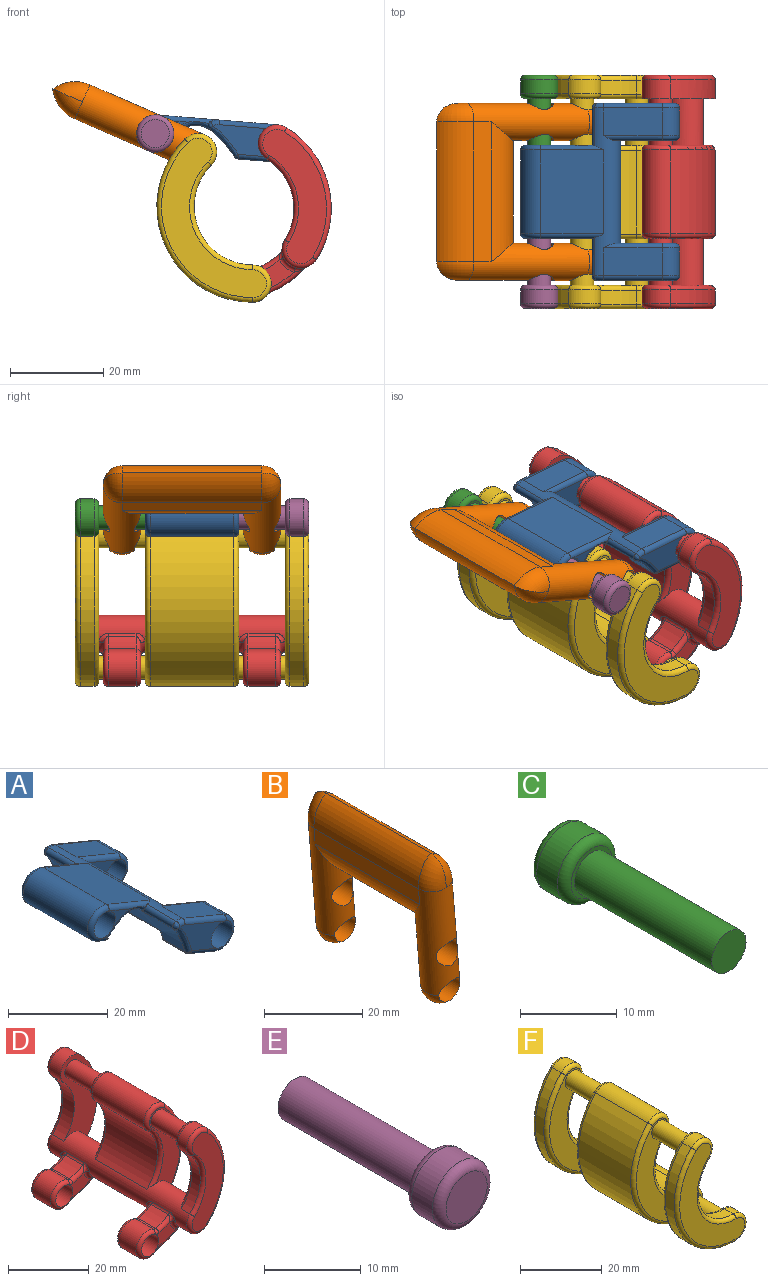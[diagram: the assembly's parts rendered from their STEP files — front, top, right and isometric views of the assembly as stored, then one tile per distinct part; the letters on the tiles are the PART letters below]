
ASSEMBLY  parts=6 mates=6
PART A: 60 faces, bbox 32.8x38x18.6 mm
  f0: plane 18x12.5mm, normal (0.38,0,0.92), area 243.4mm2, adj f2,f6,f49,f52
  f1: plane 18x1.85mm, normal (-0.38,0,-0.92), area 36.1mm2, adj f2,f51,f54,f57
  f2: cylinder r=4mm len=18mm, axis (0,1,0), area 226.2mm2, adj f0,f1,f50,f53
  f3: cylinder r=3mm len=20mm, axis (0,1,0), area 377mm2, adj f12,f19,f50,f53
  f4: extruded ~36x13.26mm, area 432.7mm2, adj f22,f27,f31,f34,f36,f38,f40,f43
  f5: plane 7.38x6mm, normal (-0.38,0,-0.92), area 47.9mm2, adj f9,f26,f30,f31
  f6: cylinder r=4mm len=36mm, axis (0,-1,0), area 200.1mm2, adj f0,f8,f11,f15,f18,f21,f22,f25
  f7: plane 13.07x10.59mm, normal (0,1,0), area 50.4mm2, adj f10,f20,f21,f26,f27
  f8: plane 10.18x9.36mm, normal (0,-1,0), area 38.9mm2, adj f6,f10,f25,f30,f34,f36
  f9: cylinder r=4mm len=7.7mm, axis (0,-1,0), area 75.4mm2, adj f5,f11,f23,f28
  f10: cylinder r=3mm len=8mm, axis (0,-1,0), area 150.8mm2, adj f7,f8,f23,f28
  f11: plane 11.67x6mm, normal (0.38,0,0.92), area 75.7mm2, adj f6,f9,f20,f25
  f12: plane 8.44x6.31mm, normal (0,1,0), area 8.5mm2, adj f3,f49,f51,f59
  f13: plane 7.38x6mm, normal (-0.38,0,-0.92), area 47.9mm2, adj f16,f37,f40,f42
  f14: plane 13.07x10.59mm, normal (0,-1,0), area 50.4mm2, adj f17,f42,f43,f47,f48
  f15: plane 10.18x9.36mm, normal (0,1,0), area 38.9mm2, adj f6,f17,f33,f36,f37,f38
  f16: cylinder r=4mm len=7.7mm, axis (0,1,0), area 75.4mm2, adj f13,f18,f35,f45
  f17: cylinder r=3mm len=8mm, axis (0,1,0), area 150.8mm2, adj f14,f15,f35,f45
  f18: plane 11.67x6mm, normal (0.38,0,0.92), area 75.7mm2, adj f6,f16,f33,f47
  f19: plane 8.44x6.31mm, normal (0,-1,0), area 8.5mm2, adj f3,f52,f54,f55
  f20: cylinder r=1mm len=12.05mm, axis (-0.92,0,0.38), area 19.8mm2, adj f7,f11,f21,f23
  f21: torus R=3mm, axis (0,1,0), area 2.7mm2, adj f6,f7,f20,f24
  f22: cylinder r=1mm len=9mm, axis (0,-1,0), area 18.2mm2, adj f4,f6,f24,f49,f59
  f23: torus R=3mm, axis (0,1,0), area 17.9mm2, adj f9,f10,f20,f26
  f24: sphere r=1mm, area 1.5mm2, adj f21,f22,f27
  f25: cylinder r=1mm len=12.05mm, axis (0.92,0,-0.38), area 17.8mm2, adj f6,f8,f11,f28
  f26: cylinder r=1mm len=7.76mm, axis (0.92,0,-0.38), area 12.5mm2, adj f5,f7,f23,f29
  f27: bspline ~9.21x4.77mm, area 12.6mm2, adj f4,f7,f24,f29
  f28: torus R=3mm, axis (0,1,0), area 17.9mm2, adj f9,f10,f25,f30
  f29: sphere r=1mm, area 0.6mm2, adj f26,f27,f31
  f30: cylinder r=1mm len=7.76mm, axis (-0.92,0,0.38), area 12.5mm2, adj f5,f8,f28,f32
  f31: cylinder r=1mm len=6mm, axis (0,-1,0), area 5.5mm2, adj f4,f5,f29,f32
  f32: sphere r=1mm, area 0.6mm2, adj f30,f31,f34
  f33: cylinder r=1mm len=12.05mm, axis (0.92,0,-0.38), area 17.8mm2, adj f6,f15,f18,f35
  f34: bspline ~5.09x2.5mm, area 3.5mm2, adj f4,f8,f32,f36
  f35: torus R=3mm, axis (0,-1,0), area 17.9mm2, adj f16,f17,f33,f37
  f36: cylinder r=1mm len=24mm, axis (0,-1,0), area 47.9mm2, adj f4,f6,f8,f15,f34,f38
  f37: cylinder r=1mm len=7.76mm, axis (-0.92,0,0.38), area 12.5mm2, adj f13,f15,f35,f39
  f38: bspline ~4.84x2.4mm, area 3.5mm2, adj f4,f15,f36,f39
  f39: sphere r=1mm, area 0.6mm2, adj f37,f38,f40
  f40: cylinder r=1mm len=6mm, axis (0,-1,0), area 5.5mm2, adj f4,f13,f39,f41
  f41: sphere r=1mm, area 0.6mm2, adj f40,f42,f43
  f42: cylinder r=1mm len=7.76mm, axis (0.92,0,-0.38), area 12.5mm2, adj f13,f14,f41,f45
  f43: bspline ~9.21x4.77mm, area 12.6mm2, adj f4,f14,f41,f46
  f44: cylinder r=1mm len=9mm, axis (0,-1,0), area 18.2mm2, adj f4,f6,f46,f52,f55
  f45: torus R=3mm, axis (0,-1,0), area 17.9mm2, adj f16,f17,f42,f47
  f46: sphere r=1mm, area 1.5mm2, adj f43,f44,f48
  f47: cylinder r=1mm len=12.05mm, axis (-0.92,0,0.38), area 19.8mm2, adj f14,f18,f45,f48
  f48: torus R=3mm, axis (0,-1,0), area 2.7mm2, adj f6,f14,f46,f47
  f49: cylinder r=1mm len=12.88mm, axis (-0.92,0,0.38), area 18.2mm2, adj f0,f6,f12,f22,f50,f59
  f50: torus R=3mm, axis (0,1,0), area 17.9mm2, adj f2,f3,f49,f51
  f51: cylinder r=1mm len=2.23mm, axis (0.92,0,-0.38), area 3.1mm2, adj f1,f12,f50,f58
  f52: cylinder r=1mm len=12.88mm, axis (-0.92,0,0.38), area 18.2mm2, adj f0,f6,f19,f44,f53,f55
  f53: torus R=3mm, axis (0,-1,0), area 17.9mm2, adj f2,f3,f52,f54
  f54: cylinder r=1mm len=2.23mm, axis (0.92,0,-0.38), area 3.1mm2, adj f1,f19,f53,f56
  f55: bspline ~12.58x4.99mm, area 18.6mm2, adj f4,f19,f44,f52,f56
  f56: sphere r=1mm, area 1.2mm2, adj f54,f55,f57
  f57: cylinder r=1mm len=18mm, axis (0,-1,0), area 21.2mm2, adj f1,f4,f56,f58
  f58: sphere r=1mm, area 0.7mm2, adj f51,f57,f59
  f59: bspline ~12.58x4.99mm, area 18.6mm2, adj f4,f12,f22,f49,f58
PART B: 18 faces, bbox 10.9x38x38.4 mm
  f0: plane 30x3.99mm, normal (-1,0,-0.08), area 120mm2, adj f5,f7,f13,f17
  f1: plane 30x3.99mm, normal (1,0,0.08), area 120mm2, adj f4,f7,f13,f16
  f2: cylinder r=3mm len=8mm, axis (0,1,0), area 126.6mm2, adj f7
  f3: cylinder r=3mm len=8mm, axis (0,1,0), area 113.2mm2, adj f6,f7
  f4: cylinder r=8mm len=30mm, axis (0,-1,0), area 251.3mm2, adj f1,f5,f8,f14
  f5: cylinder r=8mm len=30mm, axis (0,1,0), area 251.3mm2, adj f0,f4,f9,f15
  f6: sphere r=4mm, area 66.5mm2, adj f3,f7
  f7: cylinder r=4mm len=27.59mm, axis (-0.08,0,1), area 486.8mm2, adj f0,f1,f2,f3,f6,f8,f9,f16
  f8: torus R=4mm, axis (0,-1,0), area 36.9mm2, adj f4,f7,f9
  f9: torus R=4mm, axis (0,-1,0), area 36.9mm2, adj f5,f7,f8
  f10: cylinder r=3mm len=8mm, axis (0,-1,0), area 126.6mm2, adj f13
  f11: cylinder r=3mm len=8mm, axis (0,-1,0), area 113.2mm2, adj f12,f13
  f12: sphere r=4mm, area 66.5mm2, adj f11,f13
  f13: cylinder r=4mm len=27.59mm, axis (-0.08,0,1), area 486.8mm2, adj f0,f1,f10,f11,f12,f14,f15,f16
  f14: torus R=4mm, axis (0,1,0), area 36.9mm2, adj f4,f13,f15
  f15: torus R=4mm, axis (0,1,0), area 36.9mm2, adj f5,f13,f14
  f16: cylinder r=8mm len=30mm, axis (0,-1,0), area 209.7mm2, adj f1,f7,f13,f17
  f17: cylinder r=8mm len=30mm, axis (0,1,0), area 209.7mm2, adj f0,f7,f13,f16
PART C: 7 faces, bbox 8.7x25x8.7 mm
  f0: cylinder r=2.5mm len=20mm, axis (0,-1,0), area 314.2mm2, adj f1,f4
  f1: plane 5x5mm, normal (0,-1,0), area 19.6mm2, adj f0
  f2: cylinder r=4mm len=8mm, axis (0,-1,0), area 75.4mm2, adj f5,f6
  f3: plane 6x6mm, normal (0,1,0), area 28.3mm2, adj f6
  f4: plane 6x6mm, normal (0,-1,0), area 8.6mm2, adj f0,f5
  f5: torus R=3mm, axis (0,1,0), area 35.9mm2, adj f2,f4
  f6: torus R=3mm, axis (0,1,0), area 35.9mm2, adj f2,f3
PART D: 87 faces, bbox 26.5x50x36.8 mm
  f0: plane 7.67x5.93mm, normal (0,-1,0), area 21.4mm2, adj f11,f17,f21,f23,f27,f28
  f1: plane 7.67x5.93mm, normal (0,1,0), area 21.4mm2, adj f11,f25,f30,f33,f34,f35
  f2: cylinder r=4mm len=6.83mm, axis (0,-1,0), area 50.3mm2, adj f3,f5,f7,f39
  f3: cylinder r=12.5mm len=17.68mm, axis (0,-1,0), area 78.5mm2, adj f2,f4,f7,f40
  f4: cylinder r=4mm len=48mm, axis (0,-1,0), area 719.8mm2, adj f3,f5,f7,f13,f15,f16,f17,f18
  f5: cylinder r=20.5mm len=28.99mm, axis (0,-1,0), area 128.8mm2, adj f2,f4,f7,f37
  f6: plane 29.33x10.83mm, normal (0,1,0), area 183.8mm2, adj f37,f38,f39,f40
  f7: plane 30.16x12.83mm, normal (0,-1,0), area 187.7mm2, adj f2,f3,f4,f5,f12
  f8: cylinder r=13.5mm len=6mm, axis (0,-1,0), area 29.7mm2, adj f20,f21,f30,f31
  f9: cylinder r=4mm len=8mm, axis (0,-1,0), area 106mm2, adj f22,f31,f32,f36
  f10: cylinder r=19.5mm len=8.19mm, axis (0,-1,0), area 53.7mm2, adj f23,f24,f32,f33
  f11: cylinder r=3mm len=8mm, axis (0,-1,0), area 150.8mm2, adj f0,f1,f22,f36
  f12: cylinder r=2.5mm len=10mm, axis (0,-1,0), area 157.1mm2, adj f7,f16
  f13: cylinder r=20.5mm len=28.99mm, axis (0,-1,0), area 579.6mm2, adj f4,f14,f41,f86
  f14: cylinder r=4mm len=18mm, axis (0,-1,0), area 226.2mm2, adj f13,f15,f42,f85
  f15: cylinder r=12.5mm len=18mm, axis (0,-1,0), area 353.4mm2, adj f4,f14,f43,f84
  f16: plane 26.28x10.83mm, normal (0,1,0), area 128.5mm2, adj f4,f12,f41,f42,f43
  f17: torus R=5mm, axis (0,1,0), area 5.7mm2, adj f0,f4,f18,f19
  f18: bspline ~2.2x2.09mm, area 2.6mm2, adj f4,f17,f20,f21
  f19: bspline ~2.97x2.17mm, area 2.8mm2, adj f4,f17,f23,f24
  f20: cylinder r=1mm len=6mm, axis (0,-1,0), area 4.5mm2, adj f4,f8,f18,f26
  f21: torus R=14.5mm, axis (0,1,0), area 7mm2, adj f0,f8,f18,f27
  f22: torus R=3mm, axis (0,1,0), area 25.2mm2, adj f9,f11,f27,f28
  f23: torus R=18.5mm, axis (0,1,0), area 12.5mm2, adj f0,f10,f19,f28
  f24: cylinder r=1mm len=6mm, axis (0,1,0), area 3.4mm2, adj f4,f10,f19,f29
  f25: torus R=5mm, axis (0,1,0), area 5.7mm2, adj f1,f4,f26,f29
  f26: bspline ~2.31x2.31mm, area 2.6mm2, adj f4,f20,f25,f30
  f27: torus R=2mm, axis (0,1,0), area 1.6mm2, adj f0,f21,f22,f31
  f28: torus R=2mm, axis (0,1,0), area 1.2mm2, adj f0,f22,f23,f32
  f29: bspline ~2.93x2.3mm, area 2.8mm2, adj f4,f24,f25,f33
  f30: torus R=14.5mm, axis (0,1,0), area 7mm2, adj f1,f8,f26,f34
  f31: cylinder r=1mm len=6mm, axis (0,-1,0), area 4.5mm2, adj f8,f9,f27,f34
  f32: cylinder r=1mm len=6mm, axis (0,1,0), area 3.4mm2, adj f9,f10,f28,f35
  f33: torus R=18.5mm, axis (0,1,0), area 12.5mm2, adj f1,f10,f29,f35
  f34: torus R=2mm, axis (0,1,0), area 1.6mm2, adj f1,f30,f31,f36
  f35: torus R=2mm, axis (0,1,0), area 1.2mm2, adj f1,f32,f33,f36
  f36: torus R=3mm, axis (0,1,0), area 25.2mm2, adj f9,f11,f34,f35
  f37: torus R=19.5mm, axis (0,1,0), area 49.7mm2, adj f5,f6,f38,f39
  f38: torus R=3mm, axis (0,1,0), area 17.9mm2, adj f4,f6,f37,f40
  f39: torus R=3mm, axis (0,1,0), area 17.9mm2, adj f2,f6,f37,f40
  f40: torus R=13.5mm, axis (0,1,0), area 31.7mm2, adj f3,f6,f38,f39
  f41: torus R=19.5mm, axis (0,1,0), area 47.4mm2, adj f4,f13,f16,f42
  f42: torus R=3mm, axis (0,1,0), area 17.9mm2, adj f14,f16,f41,f43
  f43: torus R=13.5mm, axis (0,1,0), area 29.9mm2, adj f4,f15,f16,f42
  f44: plane 7.67x5.93mm, normal (0,1,0), area 21.4mm2, adj f54,f57,f60,f64,f66,f69
  f45: plane 7.67x5.93mm, normal (0,-1,0), area 21.4mm2, adj f54,f62,f71,f72,f74,f75
  f46: cylinder r=4mm len=6.83mm, axis (0,1,0), area 37.7mm2, adj f47,f48,f79,f83
  f47: cylinder r=12.5mm len=17.68mm, axis (0,1,0), area 58.9mm2, adj f4,f46,f77,f82
  f48: cylinder r=20.5mm len=28.99mm, axis (0,1,0), area 96.6mm2, adj f4,f46,f80,f81
  f49: plane 29.33x10.83mm, normal (0,-1,0), area 183.8mm2, adj f77,f78,f79,f80
  f50: plane 26.28x10.83mm, normal (0,1,0), area 128.5mm2, adj f4,f55,f81,f82,f83
  f51: cylinder r=13.5mm len=6mm, axis (0,1,0), area 29.7mm2, adj f60,f61,f70,f71
  f52: cylinder r=4mm len=8mm, axis (0,1,0), area 106mm2, adj f65,f70,f73,f76
  f53: cylinder r=19.5mm len=8.19mm, axis (0,1,0), area 53.7mm2, adj f63,f64,f72,f73
  f54: cylinder r=3mm len=8mm, axis (0,1,0), area 150.8mm2, adj f44,f45,f65,f76
  f55: cylinder r=2.5mm len=10mm, axis (0,1,0), area 157.1mm2, adj f50,f56
  f56: plane 26.28x10.83mm, normal (0,-1,0), area 128.5mm2, adj f4,f55,f84,f85,f86
  f57: torus R=5mm, axis (0,-1,0), area 5.7mm2, adj f4,f44,f58,f59
  f58: bspline ~2.31x2.31mm, area 2.6mm2, adj f4,f57,f60,f61
  f59: bspline ~2.93x2.3mm, area 2.8mm2, adj f4,f57,f63,f64
  f60: torus R=14.5mm, axis (0,-1,0), area 7mm2, adj f44,f51,f58,f66
  f61: cylinder r=1mm len=6mm, axis (0,1,0), area 4.5mm2, adj f4,f51,f58,f67
  f62: torus R=5mm, axis (0,-1,0), area 5.7mm2, adj f4,f45,f67,f68
  f63: cylinder r=1mm len=6mm, axis (0,-1,0), area 3.4mm2, adj f4,f53,f59,f68
  f64: torus R=18.5mm, axis (0,-1,0), area 12.5mm2, adj f44,f53,f59,f69
  f65: torus R=3mm, axis (0,-1,0), area 25.2mm2, adj f52,f54,f66,f69
  f66: torus R=2mm, axis (0,-1,0), area 1.6mm2, adj f44,f60,f65,f70
  f67: bspline ~2.2x2.09mm, area 2.6mm2, adj f4,f61,f62,f71
  f68: bspline ~2.97x2.17mm, area 2.8mm2, adj f4,f62,f63,f72
  f69: torus R=2mm, axis (0,-1,0), area 1.2mm2, adj f44,f64,f65,f73
  f70: cylinder r=1mm len=6mm, axis (0,1,0), area 4.5mm2, adj f51,f52,f66,f74
  f71: torus R=14.5mm, axis (0,-1,0), area 7mm2, adj f45,f51,f67,f74
  f72: torus R=18.5mm, axis (0,-1,0), area 12.5mm2, adj f45,f53,f68,f75
  f73: cylinder r=1mm len=6mm, axis (0,-1,0), area 3.4mm2, adj f52,f53,f69,f75
  f74: torus R=2mm, axis (0,-1,0), area 1.6mm2, adj f45,f70,f71,f76
  f75: torus R=2mm, axis (0,-1,0), area 1.2mm2, adj f45,f72,f73,f76
  f76: torus R=3mm, axis (0,-1,0), area 25.2mm2, adj f52,f54,f74,f75
  f77: torus R=13.5mm, axis (0,-1,0), area 31.7mm2, adj f47,f49,f78,f79
  f78: torus R=3mm, axis (0,-1,0), area 17.9mm2, adj f4,f49,f77,f80
  f79: torus R=3mm, axis (0,-1,0), area 17.9mm2, adj f46,f49,f77,f80
  f80: torus R=19.5mm, axis (0,-1,0), area 49.7mm2, adj f48,f49,f78,f79
  f81: torus R=19.5mm, axis (0,-1,0), area 47.4mm2, adj f4,f48,f50,f83
  f82: torus R=13.5mm, axis (0,-1,0), area 29.9mm2, adj f4,f47,f50,f83
  f83: torus R=3mm, axis (0,-1,0), area 17.9mm2, adj f46,f50,f81,f82
  f84: torus R=13.5mm, axis (0,-1,0), area 29.9mm2, adj f4,f15,f56,f85
  f85: torus R=3mm, axis (0,-1,0), area 17.9mm2, adj f14,f56,f84,f86
  f86: torus R=19.5mm, axis (0,-1,0), area 47.4mm2, adj f4,f13,f56,f85
PART E: 7 faces, bbox 8.7x25x8.7 mm
  f0: cylinder r=2.5mm len=20mm, axis (0,1,0), area 314.2mm2, adj f1,f4
  f1: plane 5x5mm, normal (0,1,0), area 19.6mm2, adj f0
  f2: cylinder r=4mm len=8mm, axis (0,1,0), area 75.4mm2, adj f5,f6
  f3: plane 6x6mm, normal (0,-1,0), area 28.3mm2, adj f6
  f4: plane 6x6mm, normal (0,1,0), area 8.6mm2, adj f0,f5
  f5: torus R=3mm, axis (0,-1,0), area 35.9mm2, adj f2,f4
  f6: torus R=3mm, axis (0,-1,0), area 35.9mm2, adj f2,f3
PART F: 46 faces, bbox 26.5x50x38.2 mm
  f0: cylinder r=4mm len=18mm, axis (0,-1,0), area 226.2mm2, adj f1,f3,f24,f44
  f1: cylinder r=12.5mm len=21.34mm, axis (0,-1,0), area 530.1mm2, adj f0,f2,f23,f45
  f2: cylinder r=4mm len=18mm, axis (0,-1,0), area 226.2mm2, adj f1,f3,f21,f43
  f3: cylinder r=20.5mm len=35mm, axis (0,-1,0), area 869.4mm2, adj f0,f2,f22,f42
  f4: plane 34.17x22.5mm, normal (0,1,0), area 222.3mm2, adj f5,f6,f21,f22,f23,f24
  f5: cylinder r=2.5mm len=10mm, axis (0,-1,0), area 157.1mm2, adj f4,f12
  f6: cylinder r=2.5mm len=10mm, axis (0,-1,0), area 157.1mm2, adj f4,f12
  f7: cylinder r=4mm len=8mm, axis (0,-1,0), area 37.7mm2, adj f8,f10,f13,f19
  f8: cylinder r=12.5mm len=21.34mm, axis (0,-1,0), area 88.4mm2, adj f7,f9,f14,f20
  f9: cylinder r=4mm len=6.83mm, axis (0,-1,0), area 37.7mm2, adj f8,f10,f16,f18
  f10: cylinder r=20.5mm len=35mm, axis (0,-1,0), area 144.9mm2, adj f7,f9,f15,f17
  f11: plane 34.17x22.5mm, normal (0,1,0), area 261.5mm2, adj f13,f14,f15,f16
  f12: plane 34.17x22.5mm, normal (0,-1,0), area 222.3mm2, adj f5,f6,f17,f18,f19,f20
  f13: torus R=3mm, axis (0,1,0), area 17.9mm2, adj f7,f11,f14,f15
  f14: torus R=13.5mm, axis (0,1,0), area 47.6mm2, adj f8,f11,f13,f16
  f15: torus R=19.5mm, axis (0,1,0), area 74.5mm2, adj f10,f11,f13,f16
  f16: torus R=3mm, axis (0,1,0), area 17.9mm2, adj f9,f11,f14,f15
  f17: torus R=19.5mm, axis (0,1,0), area 74.5mm2, adj f10,f12,f18,f19
  f18: torus R=3mm, axis (0,1,0), area 17.9mm2, adj f9,f12,f17,f20
  f19: torus R=3mm, axis (0,1,0), area 17.9mm2, adj f7,f12,f17,f20
  f20: torus R=13.5mm, axis (0,1,0), area 47.6mm2, adj f8,f12,f18,f19
  f21: torus R=3mm, axis (0,1,0), area 17.9mm2, adj f2,f4,f22,f23
  f22: torus R=19.5mm, axis (0,1,0), area 74.5mm2, adj f3,f4,f21,f24
  f23: torus R=13.5mm, axis (0,1,0), area 47.6mm2, adj f1,f4,f21,f24
  f24: torus R=3mm, axis (0,1,0), area 17.9mm2, adj f0,f4,f22,f23
  f25: plane 34.17x22.5mm, normal (0,-1,0), area 222.3mm2, adj f26,f27,f42,f43,f44,f45
  f26: cylinder r=2.5mm len=10mm, axis (0,1,0), area 157.1mm2, adj f25,f33
  f27: cylinder r=2.5mm len=10mm, axis (0,1,0), area 157.1mm2, adj f25,f33
  f28: cylinder r=4mm len=8mm, axis (0,1,0), area 37.7mm2, adj f29,f31,f36,f40
  f29: cylinder r=12.5mm len=21.34mm, axis (0,1,0), area 88.4mm2, adj f28,f30,f34,f41
  f30: cylinder r=4mm len=6.83mm, axis (0,1,0), area 37.7mm2, adj f29,f31,f35,f39
  f31: cylinder r=20.5mm len=35mm, axis (0,1,0), area 144.9mm2, adj f28,f30,f37,f38
  f32: plane 34.17x22.5mm, normal (0,-1,0), area 261.5mm2, adj f34,f35,f36,f37
  f33: plane 34.17x22.5mm, normal (0,1,0), area 222.3mm2, adj f26,f27,f38,f39,f40,f41
  f34: torus R=13.5mm, axis (0,-1,0), area 47.6mm2, adj f29,f32,f35,f36
  f35: torus R=3mm, axis (0,-1,0), area 17.9mm2, adj f30,f32,f34,f37
  f36: torus R=3mm, axis (0,-1,0), area 17.9mm2, adj f28,f32,f34,f37
  f37: torus R=19.5mm, axis (0,-1,0), area 74.5mm2, adj f31,f32,f35,f36
  f38: torus R=19.5mm, axis (0,-1,0), area 74.5mm2, adj f31,f33,f39,f40
  f39: torus R=3mm, axis (0,-1,0), area 17.9mm2, adj f30,f33,f38,f41
  f40: torus R=3mm, axis (0,-1,0), area 17.9mm2, adj f28,f33,f38,f41
  f41: torus R=13.5mm, axis (0,-1,0), area 47.6mm2, adj f29,f33,f39,f40
  f42: torus R=19.5mm, axis (0,-1,0), area 74.5mm2, adj f3,f25,f43,f44
  f43: torus R=3mm, axis (0,-1,0), area 17.9mm2, adj f2,f25,f42,f45
  f44: torus R=3mm, axis (0,-1,0), area 17.9mm2, adj f0,f25,f42,f45
  f45: torus R=13.5mm, axis (0,-1,0), area 47.6mm2, adj f1,f25,f43,f44
PLACE A rot(axis=(0,-1,0),17.8deg) t=(-2.34,0,-1.13)mm
PLACE B rot(axis=(0,-1,0),61.7deg) t=(4.14,0,16.41)mm
PLACE C rot(axis=(0,-1,0),52deg) t=(3.9,0,12.17)mm
PLACE D rot(axis=(0,-1,0),12.7deg) t=(-3.62,0,-0.4)mm
PLACE E rot(axis=(0,-1,0),52deg) t=(3.9,0,12.17)mm
PLACE F at identity fixed
MATE revolute B.f2 <-> E.f0  axis (0,1,0) through (-20.85,-15,15.67)mm
MATE revolute A.f9 <-> D.f2  axis (0,-1,0) through (5.21,15,13.54)mm
MATE fastened C.f0 <-> E.f0  axis (0,-1,0) through (-20.85,0,15.67)mm
MATE revolute C.f0 <-> A.f2  axis (0,-1,0) through (-20.85,0,15.67)mm
MATE revolute D.f9 <-> F.f6  axis (0,1,0) through (0,-15,-16.5)mm
MATE revolute B.f3 <-> F.f2  axis (0,1,0) through (-11.67,-15,11.67)mm
